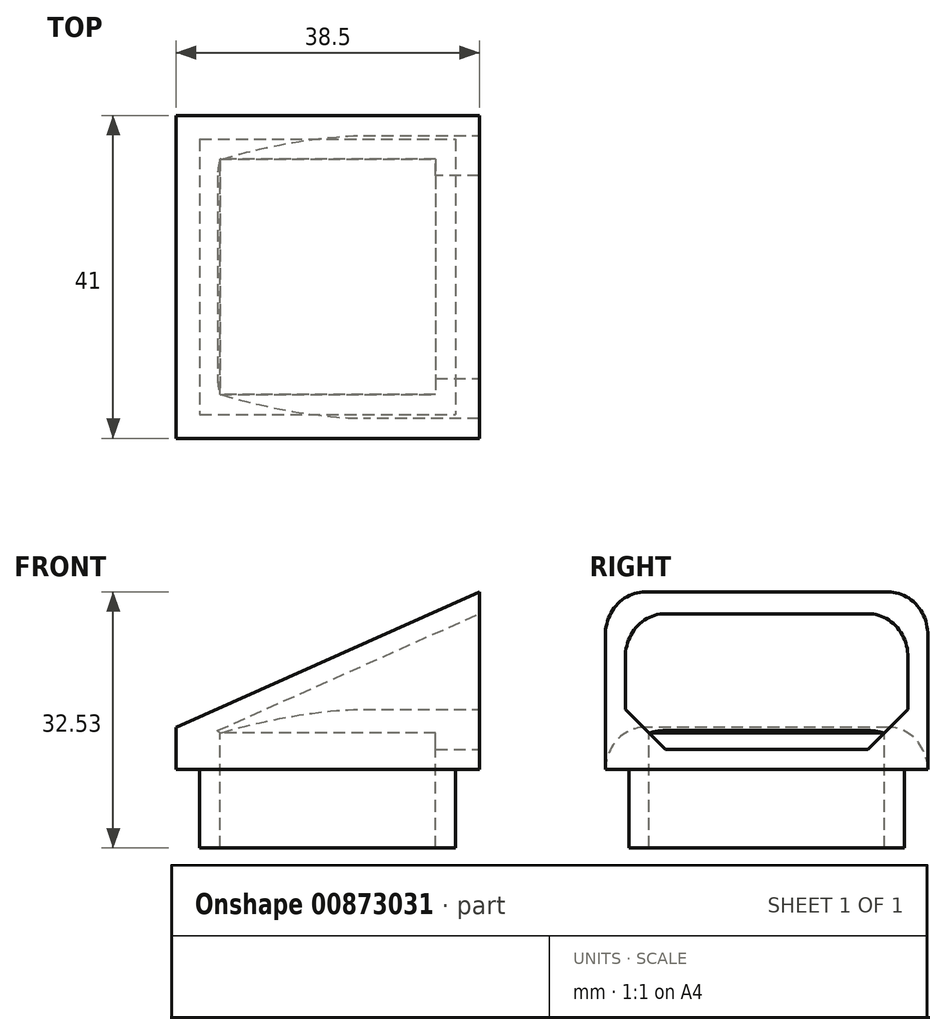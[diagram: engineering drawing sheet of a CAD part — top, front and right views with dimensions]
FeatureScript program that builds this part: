
annotation { "Feature Type Name" : "Feature", "Feature Type Description" : "" }
export const myFeature = defineFeature(function(context is Context, id is Id, definition is map)
    precondition{}
    {
        {
            var Q0;
            Q0=qCreatedBy(makeId("Top.planeOp"),FACE);
            var sketch = newSketch(context, id + "F0", { "sketchPlane" : qUnion([Q0])});
            skLineSegment(sketch, "E0.bottom", {"start": v(-38.5, 20.5) * mm, "end": v(0, 20.5) * mm});
            skLineSegment(sketch, "E0.top", {"start": v(-38.5, -20.5) * mm, "end": v(0, -20.5) * mm});
            skLineSegment(sketch, "E0.left", {"start": v(-38.5, 20.5) * mm, "end": v(-38.5, -20.5) * mm});
            skLineSegment(sketch, "E0.right", {"start": v(0, 20.5) * mm, "end": v(0, -20.5) * mm});
            skSolve(sketch);
        }
        {
            var Q0;
            Q0=makeQuery(id+"F0.imprint","IMPRINT",FACE,{"disambiguationData":[TD([[makeQuery(id+"F0.imprint","IMPRINT",EDGE,{"derivedFrom":sQuery(id+"F0.wireOp",EDGE,"E0.bottom")}),-1.0]])]});
            extrude(context, id + "F1", {"entities" : qUnion([Q0]), "depth" : 5.33 * mm, "offsetDistance" : 25.4 * mm});
        }
        {
            var Q0;
            Q0=qCreatedBy(makeId("Right.planeOp"),FACE);
            var sketch = newSketch(context, id + "F2", { "sketchPlane" : qUnion([Q0])});
            skLineSegment(sketch, "E1.bottom", {"start": v(-20.5, 12.41) * mm, "end": v(20.5, 12.41) * mm});
            skLineSegment(sketch, "E1.top", {"start": v(-20.5, 22.53) * mm, "end": v(20.5, 22.53) * mm});
            skLineSegment(sketch, "E1.left", {"start": v(-20.5, 12.41) * mm, "end": v(-20.5, 22.53) * mm});
            skLineSegment(sketch, "E1.right", {"start": v(20.5, 12.41) * mm, "end": v(20.5, 22.53) * mm});
            skSolve(sketch);
        }
        {
            var Q0;
            Q0=makeQuery(id+"F1.opExtrude","CAP_FACE",FACE,{"disambiguationData":[OSD([sQuery(id+"F0.wireOp",EDGE,"E0.bottom"),sQuery(id+"F0.wireOp",EDGE,"E0.top"),sQuery(id+"F0.wireOp",EDGE,"E0.left"),sQuery(id+"F0.wireOp",EDGE,"E0.right")])],"isStart":true});
            var sketch = newSketch(context, id + "F3", { "sketchPlane" : qUnion([Q0])});
            skLineSegment(sketch, "E2.0", {"start": v(-3, -17.5) * mm, "end": v(-3, 17.5) * mm});
            skLineSegment(sketch, "E2.1", {"start": v(-35.5, -17.5) * mm, "end": v(-3, -17.5) * mm});
            skLineSegment(sketch, "E2.2", {"start": v(-35.5, -17.5) * mm, "end": v(-35.5, 17.5) * mm});
            skLineSegment(sketch, "E2.3", {"start": v(-35.5, 17.5) * mm, "end": v(-3, 17.5) * mm});
            skSolve(sketch);
        }
        {
            var Q0;
            Q0=makeQuery(id+"F3.imprint","IMPRINT",FACE,{"disambiguationData":[TD([[makeQuery(id+"F3.imprint","IMPRINT",EDGE,{"derivedFrom":sQuery(id+"F3.wireOp",EDGE,"E2.0")}),1.0]])]});
            extrude(context, id + "F4", {"entities" : qUnion([Q0]), "operationType" : NewBodyOperationType.ADD, "depth" : 10 * mm, "offsetDistance" : 25.4 * mm});
        }
        {
            var Q1;
            Q1=makeQuery(id+"F1.opExtrude","CAP_FACE",FACE,{"disambiguationData":[OSD([sQuery(id+"F0.wireOp",EDGE,"E0.bottom"),sQuery(id+"F0.wireOp",EDGE,"E0.top"),sQuery(id+"F0.wireOp",EDGE,"E0.left"),sQuery(id+"F0.wireOp",EDGE,"E0.right")])],"isStart":false});
            var Q2;
            Q2=makeQuery(id+"F2.imprint","IMPRINT",FACE,{"disambiguationData":[TD([[makeQuery(id+"F2.imprint","IMPRINT",EDGE,{"derivedFrom":sQuery(id+"F2.wireOp",EDGE,"E1.bottom")}),1.0]])]});
            loft(context, id + "F5", {"operationType" : NewBodyOperationType.ADD, "sheetProfilesArray" : [{ "sheetProfileEntities" : qUnion([Q1]) }, { "sheetProfileEntities" : qUnion([Q2]) }]});
        }
        {
            var Q0;
            {var subQ0=sQuery(id+"F0.wireOp",EDGE,"E0.right");Q0=makeQuery(id+"F5.boolean.opBoolean","MERGE",FACE,{"derivedFrom":[makeQuery(id+"F1.opExtrude","SWEPT_FACE",FACE,{"disambiguationData":[OSD([subQ0])]}),makeQuery(id+"F5.opLoft","SWEPT_FACE",FACE,{"disambiguationData":[OSD([sQuery(id+"F0.wireOp",EDGE,"E0.bottom"),sQuery(id+"F0.wireOp",EDGE,"E0.top"),subQ0,sQuery(id+"F2.wireOp",EDGE,"E1.bottom"),sQuery(id+"F2.wireOp",EDGE,"E1.left"),sQuery(id+"F2.wireOp",EDGE,"E1.right")])]})]});}
            var Q1;
            Q1=makeQuery(id+"F4.opExtrude","CAP_FACE",FACE,{"disambiguationData":[OSD([sQuery(id+"F3.wireOp",EDGE,"E2.0"),sQuery(id+"F3.wireOp",EDGE,"E2.1"),sQuery(id+"F3.wireOp",EDGE,"E2.2"),sQuery(id+"F3.wireOp",EDGE,"E2.3")])],"isStart":false});
            shell(context, id + "F6", {"entities" : qUnion([Q0, Q1]), "thickness" : 2.54 * mm});
        }
        {
            var Q0;
            Q0=makeQuery(id+"F6.opShell","OFFSET_EDGE",EDGE,{"disambiguationData":[OSD([sQuery(id+"F0.wireOp",EDGE,"E0.top")])]});
            var Q1;
            Q1=makeQuery(id+"F6.opShell","OFFSET_EDGE",EDGE,{"disambiguationData":[OSD([sQuery(id+"F0.wireOp",EDGE,"E0.left")])]});
            var Q2;
            Q2=makeQuery(id+"F6.opShell","OFFSET_EDGE",EDGE,{"disambiguationData":[OSD([sQuery(id+"F0.wireOp",EDGE,"E0.bottom")])]});
            chamfer(context, id + "F7", {"entities" : qUnion([Q0, Q1, Q2]), "width" : 5.08 * mm, "tangentPropagation" : true});
        }
        {
            var Q0;
            Q0=makeQuery(id+"F5.opLoft","SWEPT_EDGE",EDGE,{"disambiguationData":[OSD([sQuery(id+"F0.wireOp",EDGE,"E0.top"),sQuery(id+"F0.wireOp",EDGE,"E0.left"),sQuery(id+"F2.wireOp",EDGE,"E1.top"),sQuery(id+"F2.wireOp",EDGE,"E1.left")])]});
            var Q1;
            Q1=makeQuery(id+"F5.opLoft","SWEPT_EDGE",EDGE,{"disambiguationData":[OSD([sQuery(id+"F0.wireOp",EDGE,"E0.bottom"),sQuery(id+"F0.wireOp",EDGE,"E0.left"),sQuery(id+"F2.wireOp",EDGE,"E1.top"),sQuery(id+"F2.wireOp",EDGE,"E1.right")])]});
            fillet(context, id + "F8", {"entities" : qUnion([Q0, Q1]), "radius" : 5.08 * mm, "tangentPropagation" : true, "allowEdgeOverflow" : false});
        }
        {
            var Q0;
            Q0=makeQuery(id+"F6.opShell","OFFSET_EDGE",EDGE,{"disambiguationData":[OSD([sQuery(id+"F0.wireOp",EDGE,"E0.top"),sQuery(id+"F0.wireOp",EDGE,"E0.left"),sQuery(id+"F2.wireOp",EDGE,"E1.top"),sQuery(id+"F2.wireOp",EDGE,"E1.left")])]});
            var Q1;
            Q1=makeQuery(id+"F6.opShell","OFFSET_EDGE",EDGE,{"disambiguationData":[OSD([sQuery(id+"F0.wireOp",EDGE,"E0.bottom"),sQuery(id+"F0.wireOp",EDGE,"E0.left"),sQuery(id+"F2.wireOp",EDGE,"E1.top"),sQuery(id+"F2.wireOp",EDGE,"E1.right")])]});
            fillet(context, id + "F9", {"entities" : qUnion([Q0, Q1]), "radius" : 5.08 * mm, "tangentPropagation" : true, "allowEdgeOverflow" : false});
        }
    });
